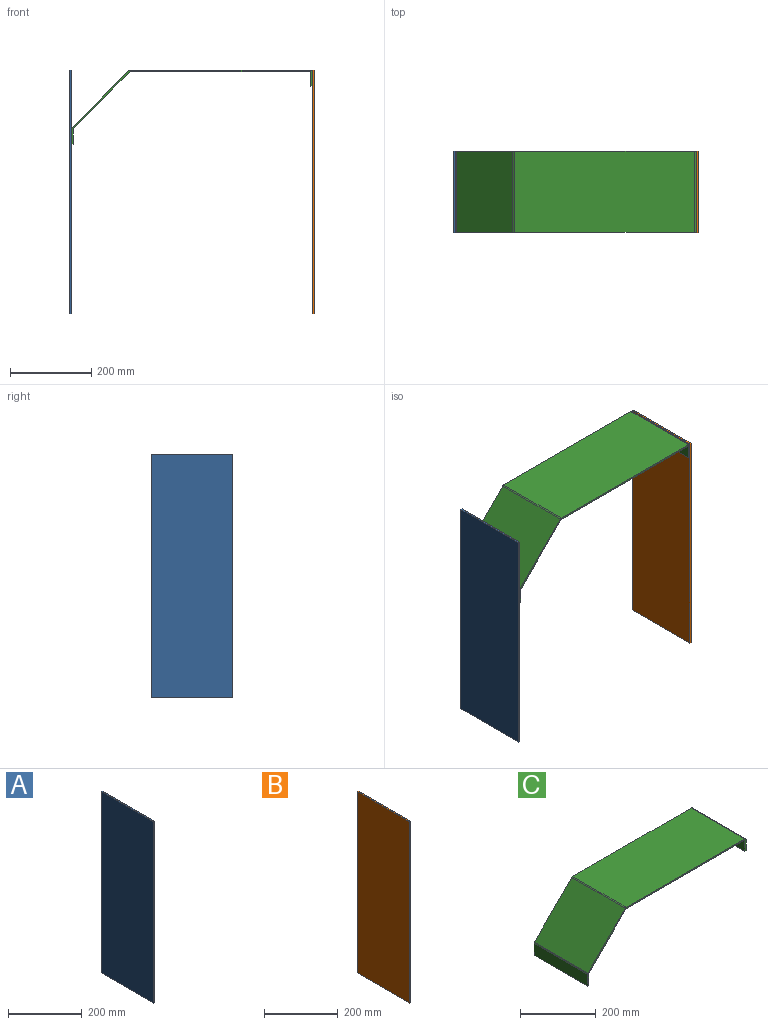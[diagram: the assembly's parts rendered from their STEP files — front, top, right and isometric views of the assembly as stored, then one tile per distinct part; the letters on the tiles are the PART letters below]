
ASSEMBLY  parts=3 mates=4
PART A: 6 faces, bbox 4x200x600 mm
  f0: plane 200x4mm, normal (0,0,1), area 800mm2, adj f1,f3,f4,f5
  f1: plane 600x4mm, normal (0,1,0), area 2400mm2, adj f0,f2,f4,f5
  f2: plane 200x4mm, normal (0,0,-1), area 800mm2, adj f1,f3,f4,f5
  f3: plane 600x4mm, normal (0,-1,0), area 2400mm2, adj f0,f2,f4,f5
  f4: plane 600x200mm, normal (-1,0,0), area 120000mm2, adj f0,f1,f2,f3
  f5: plane 600x200mm, normal (1,0,0), area 120000mm2, adj f0,f1,f2,f3
PART B: 6 faces, bbox 4x200x600 mm
  f0: plane 200x4mm, normal (0,0,1), area 800mm2, adj f1,f3,f4,f5
  f1: plane 600x4mm, normal (0,1,0), area 2400mm2, adj f0,f2,f4,f5
  f2: plane 200x4mm, normal (0,0,-1), area 800mm2, adj f1,f3,f4,f5
  f3: plane 600x4mm, normal (0,-1,0), area 2400mm2, adj f0,f2,f4,f5
  f4: plane 600x200mm, normal (-1,0,0), area 120000mm2, adj f0,f1,f2,f3
  f5: plane 600x200mm, normal (1,0,0), area 120000mm2, adj f0,f1,f2,f3
PART C: 30 faces, bbox 592.2x200x182.6 mm
  f0: plane 442.59x4mm, normal (0,1,0), area 1770.3mm2, adj f2,f3,f18,f26
  f1: plane 442.59x4mm, normal (0,-1,0), area 1770.3mm2, adj f2,f3,f17,f27
  f2: plane 442.59x200mm, normal (0,0,-1), area 88517.2mm2, adj f0,f1,f20,f29
  f3: plane 442.59x200mm, normal (0,0,1), area 88517.2mm2, adj f0,f1,f19,f28
  f4: plane 142.49x142.49mm, normal (0,1,0), area 790.1mm2, adj f6,f7,f13,f18
  f5: plane 142.49x142.49mm, normal (0,-1,0), area 790.1mm2, adj f6,f7,f14,f17
  f6: plane 200x139.66mm, normal (0.71,0,-0.71), area 39502.9mm2, adj f4,f5,f16,f20
  f7: plane 200x139.66mm, normal (-0.71,0,0.71), area 39502.9mm2, adj f4,f5,f15,f19
  f8: plane 200x4mm, normal (0,0,-1), area 800mm2, adj f9,f10,f11,f12
  f9: plane 37.93x4mm, normal (0,1,0), area 151.7mm2, adj f8,f11,f12,f13
  f10: plane 37.93x4mm, normal (0,-1,0), area 151.7mm2, adj f8,f11,f12,f14
  f11: plane 200x37.93mm, normal (1,0,0), area 7585.8mm2, adj f8,f9,f10,f16
  f12: plane 200x37.93mm, normal (-1,0,0), area 7585.8mm2, adj f8,f9,f10,f15
  f13: plane 4.29x3.54mm, normal (0,1,0), area 9.4mm2, adj f4,f9,f15,f16
  f14: plane 4.29x3.54mm, normal (0,-1,0), area 9.4mm2, adj f5,f10,f15,f16
  f15: cylinder r=5mm len=200mm, axis (0,1,0), area 785.4mm2, adj f7,f12,f13,f14
  f16: cylinder r=1mm len=200mm, axis (0,1,0), area 157.1mm2, adj f6,f11,f13,f14
  f17: plane 4.29x3.54mm, normal (0,-1,0), area 9.4mm2, adj f1,f5,f19,f20
  f18: plane 4.29x3.54mm, normal (0,1,0), area 9.4mm2, adj f0,f4,f19,f20
  f19: cylinder r=5mm len=200mm, axis (0,-1,0), area 785.4mm2, adj f3,f7,f17,f18
  f20: cylinder r=1mm len=200mm, axis (0,-1,0), area 157.1mm2, adj f2,f6,f17,f18
  f21: plane 200x4mm, normal (0,0,-1), area 800mm2, adj f22,f23,f24,f25
  f22: plane 35x4mm, normal (0,-1,0), area 140mm2, adj f21,f24,f25,f27
  f23: plane 35x4mm, normal (0,1,0), area 140mm2, adj f21,f24,f25,f26
  f24: plane 200x35mm, normal (-1,0,0), area 7000mm2, adj f21,f22,f23,f29
  f25: plane 200x35mm, normal (1,0,0), area 7000mm2, adj f21,f22,f23,f28
  f26: plane 5x5mm, normal (0,1,0), area 18.8mm2, adj f0,f23,f28,f29
  f27: plane 5x5mm, normal (0,-1,0), area 18.8mm2, adj f1,f22,f28,f29
  f28: cylinder r=5mm len=200mm, axis (0,1,0), area 1570.8mm2, adj f3,f25,f26,f27
  f29: cylinder r=1mm len=200mm, axis (0,1,0), area 314.2mm2, adj f2,f24,f26,f27
PLACE A t=(-523.81,-204.34,3.39)mm
PLACE B t=(76.44,-204.34,3.39)mm
PLACE C t=(-149.56,-204.34,599.39)mm
MATE planar B.f4 <-> C.f25  axis (-1,0,0) through (76.44,-204.34,303.39)mm
MATE planar A.f5 <-> C.f12  axis (1,0,0) through (-515.81,-204.34,303.39)mm
MATE planar C.f3 <-> B.f0  axis (0,0,1) through (-149.85,-204.34,603.39)mm
MATE planar C.f3 <-> A.f0  axis (0,0,1) through (-149.85,-204.34,603.39)mm
